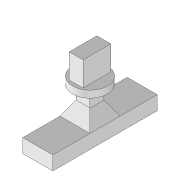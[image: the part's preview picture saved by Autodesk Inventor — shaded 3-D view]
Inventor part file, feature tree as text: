
AUTODESK INVENTOR PART (.ipt)
format: ipt  version: 2020 (Build 240168000, 168)  size: 624,640 bytes
history: native  units: mm
features: extrude x6, sketch x6, chamfer x1, fillet x1, projected_geometry x1
ambient origin geometry x8: Origin, YZ Plane, XZ Plane, XY Plane, X Axis, Y Axis, Z Axis, Center Point
bodies: Volumenkörper1 (feature_tree)
feature tree (15):
  extrude  "Extrusion1"  Depth=40.0mm
  extrude  "Extrusion2"  Depth=50.0mm
  extrude  "Extrusion3"  Depth=20.0mm
  extrude  "Extrusion4"  Depth=20.0mm TaperAngle=0.0deg
  extrude  "Extrusion5"  Depth=150.0mm
  chamfer  "Fase1"  Distance=60.0mm
  extrude  "Extrusion6"  Depth=10.0mm
  fillet  "Rundung1"  Radius=140.0mm
  sketch  "Skizze1"  dims[d0=20.0mm d1=40.0mm]
  sketch  "Skizze2"  dims[d2=35.0mm d3=0.0mm d4=50.0mm]
  sketch  "Skizze3"  dims[d5=10.0mm d6=0.0mm d7=20.0mm]
  sketch  "Skizze4"  dims[d8=20.0mm d9=20.0mm d10=0.0mm]
  projected_geometry  "Projizierte Kontur1"
  sketch  "Skizze5"  dims[d11=20.0mm d12=30.0deg d13=150.0mm d14=60.0mm d15=0.0mm]
  sketch  "Skizze6"  dims[d16=30.0mm d17=2.0mm d18=45.0deg d19=10.0mm d20=140.0mm d22=10.0mm d23=10.0mm d25=10.0mm d27=4.0mm d28=15.0mm d29=20.0mm d30=0.0mm d31=2.0mm]
